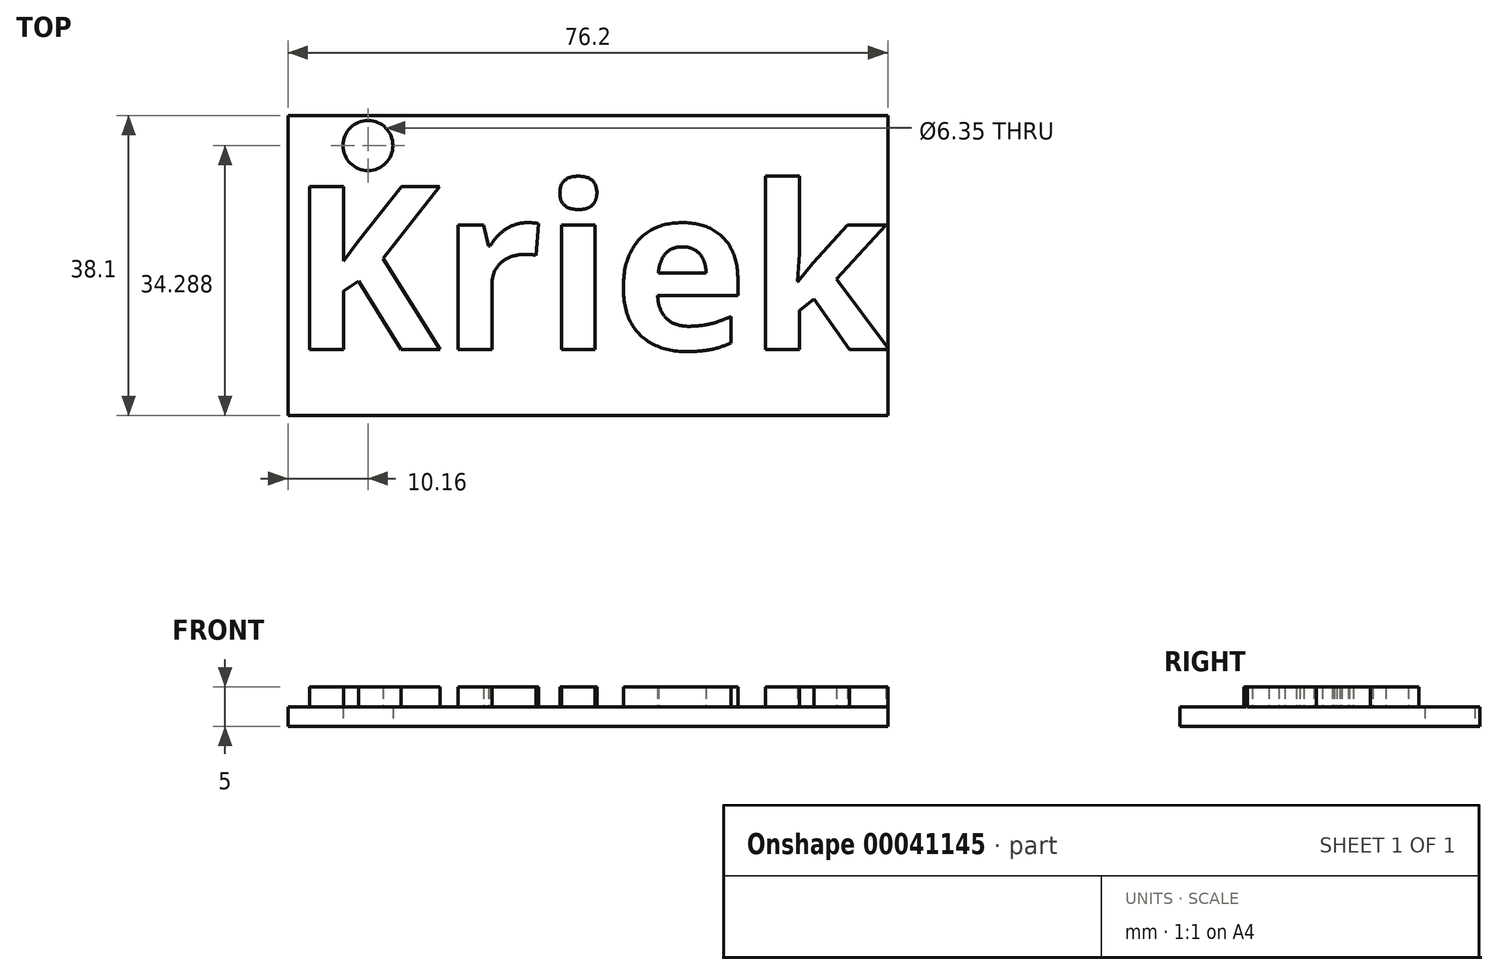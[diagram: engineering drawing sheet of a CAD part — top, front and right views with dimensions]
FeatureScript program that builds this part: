
annotation { "Feature Type Name" : "Feature", "Feature Type Description" : "" }
export const myFeature = defineFeature(function(context is Context, id is Id, definition is map)
    precondition{}
    {
        {
            var Q0;
            Q0=qCreatedBy(makeId("Top.planeOp"),FACE);
            var sketch = newSketch(context, id + "F0", { "sketchPlane" : qUnion([Q0])});
            skLineSegment(sketch, "E0.bottom", {"start": v(-38.1, 19.94) * mm, "end": v(38.1, 19.94) * mm});
            skLineSegment(sketch, "E0.top", {"start": v(-38.1, -18.16) * mm, "end": v(38.1, -18.16) * mm});
            skLineSegment(sketch, "E0.left", {"start": v(-38.1, 19.94) * mm, "end": v(-38.1, -18.16) * mm});
            skLineSegment(sketch, "E0.right", {"start": v(38.1, 19.94) * mm, "end": v(38.1, -18.16) * mm});
            skText(sketch, "E1", { "text": "Kriek", "fontName": "OpenSans-Bold.ttf"});
            skCircle(sketch, "E2", {"center": v(-27.94, 16.13) * mm, "radius": 3.18 * mm});
            const initialGuessF0  = {"E1": [-0.03798, -0.00976, 1, 0, 0.02083]};
            skSetInitialGuess(sketch, initialGuessF0);
            skSolve(sketch);
        }
        {
            var Q0;
            {var subQ5=sQuery(id+"F0.wireOp",EDGE,"E0.bottom");Q0=makeQuery(id+"F0.imprint","IMPRINT",FACE,{"disambiguationData":[TD([[makeQuery(id+"F0.imprint","IMPRINT",EDGE,{"derivedFrom":subQ5}),-1.0]])]});}
            var Q1;
            Q1=makeQuery(id+"F0.imprint","IMPRINT",FACE,{"disambiguationData":[TD([[makeQuery(id+"F0.imprint","IMPRINT",EDGE,{"derivedFrom":sQuery(id+"F0.wireOp",EDGE,"E1.sketch_text.stroke-0")}),-1.0]])]});
            var Q2;
            Q2=makeQuery(id+"F0.imprint","IMPRINT",FACE,{"disambiguationData":[TD([[makeQuery(id+"F0.imprint","IMPRINT",EDGE,{"derivedFrom":sQuery(id+"F0.wireOp",EDGE,"E1.sketch_text.stroke-13")}),-1.0]])]});
            var Q3;
            Q3=makeQuery(id+"F0.imprint","IMPRINT",FACE,{"disambiguationData":[TD([[makeQuery(id+"F0.imprint","IMPRINT",EDGE,{"derivedFrom":sQuery(id+"F0.wireOp",EDGE,"E1.sketch_text.stroke-31")}),-1.0]])]});
            var Q4;
            Q4=makeQuery(id+"F0.imprint","IMPRINT",FACE,{"disambiguationData":[TD([[makeQuery(id+"F0.imprint","IMPRINT",EDGE,{"derivedFrom":sQuery(id+"F0.wireOp",EDGE,"E1.sketch_text.stroke-35")}),1.0]])]});
            var Q5;
            Q5=makeQuery(id+"F0.imprint","IMPRINT",FACE,{"disambiguationData":[TD([[makeQuery(id+"F0.imprint","IMPRINT",EDGE,{"derivedFrom":sQuery(id+"F0.wireOp",EDGE,"E1.sketch_text.stroke-35")}),-1.0]])]});
            var Q6;
            Q6=makeQuery(id+"F0.imprint","IMPRINT",FACE,{"disambiguationData":[TD([[makeQuery(id+"F0.imprint","IMPRINT",EDGE,{"derivedFrom":sQuery(id+"F0.wireOp",EDGE,"E1.sketch_text.stroke-55")}),-1.0]])]});
            var Q7;
            Q7=makeQuery(id+"F0.imprint","IMPRINT",FACE,{"disambiguationData":[TD([[makeQuery(id+"F0.imprint","IMPRINT",EDGE,{"derivedFrom":sQuery(id+"F0.wireOp",EDGE,"E1.sketch_text.stroke-26")}),-1.0]])]});
            extrude(context, id + "F1", {"entities" : qUnion([Q0, Q1, Q2, Q3, Q4, Q5, Q6, Q7]), "depth" : 2.5 * mm});
        }
        {
            var Q0;
            Q0=makeQuery(id+"F0.imprint","IMPRINT",FACE,{"disambiguationData":[TD([[makeQuery(id+"F0.imprint","IMPRINT",EDGE,{"derivedFrom":sQuery(id+"F0.wireOp",EDGE,"E1.sketch_text.stroke-0")}),-1.0]])]});
            var Q1;
            Q1=makeQuery(id+"F0.imprint","IMPRINT",FACE,{"disambiguationData":[TD([[makeQuery(id+"F0.imprint","IMPRINT",EDGE,{"derivedFrom":sQuery(id+"F0.wireOp",EDGE,"E1.sketch_text.stroke-13")}),-1.0]])]});
            var Q2;
            Q2=makeQuery(id+"F0.imprint","IMPRINT",FACE,{"disambiguationData":[TD([[makeQuery(id+"F0.imprint","IMPRINT",EDGE,{"derivedFrom":sQuery(id+"F0.wireOp",EDGE,"E1.sketch_text.stroke-31")}),-1.0]])]});
            var Q3;
            Q3=makeQuery(id+"F0.imprint","IMPRINT",FACE,{"disambiguationData":[TD([[makeQuery(id+"F0.imprint","IMPRINT",EDGE,{"derivedFrom":sQuery(id+"F0.wireOp",EDGE,"E1.sketch_text.stroke-26")}),-1.0]])]});
            var Q4;
            Q4=makeQuery(id+"F0.imprint","IMPRINT",FACE,{"disambiguationData":[TD([[makeQuery(id+"F0.imprint","IMPRINT",EDGE,{"derivedFrom":sQuery(id+"F0.wireOp",EDGE,"E1.sketch_text.stroke-35")}),-1.0]])]});
            var Q5;
            Q5=makeQuery(id+"F0.imprint","IMPRINT",FACE,{"disambiguationData":[TD([[makeQuery(id+"F0.imprint","IMPRINT",EDGE,{"derivedFrom":sQuery(id+"F0.wireOp",EDGE,"E1.sketch_text.stroke-55")}),-1.0]])]});
            extrude(context, id + "F2", {"entities" : qUnion([Q0, Q1, Q2, Q3, Q4, Q5]), "operationType" : NewBodyOperationType.ADD, "depth" : 5 * mm});
        }
    });
